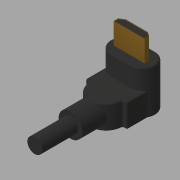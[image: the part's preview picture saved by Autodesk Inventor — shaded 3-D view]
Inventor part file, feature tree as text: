
AUTODESK INVENTOR PART (.ipt)
format: ipt  version: 2019 (Build 230136000, 136)  size: 250,880 bytes
history: native  units: mm
features: extrude x6, sketch x6, projected_geometry x3, other x2, fillet x1
ambient origin geometry x8: Origin, YZ Plane, XZ Plane, XY Plane, X Axis, Y Axis, Z Axis, Center Point
bodies: Solid1 (feature_tree), Solid2 (feature_tree)
feature tree (18):
  extrude  "Extrusion1"  Depth=7.0mm
  extrude  "Extrusion2"  Depth=15.0mm
  fillet  "Fillet1"  Radius=8.25mm
  extrude  "Extrusion3"  Depth=11.0mm
  extrude  "Extrusion4"  Depth=15.0mm
  extrude  "Extrusion5"  Depth=4.125mm
  extrude  "Extrusion6"  Depth=0.5mm
  other  "Work Axis1"
  sketch  "Sketch1"  dims[d0=14.0mm d1=7.0mm]
  sketch  "Sketch2"  dims[d2=2.0mm d3=15.0mm d4=8.25mm]
  sketch  "Sketch3"  dims[d5=4.125mm d6=11.0mm]
  projected_geometry  "Projected Loop1"
  sketch  "Sketch4"  dims[d7=8.0mm d8=0.0mm d9=15.0mm]
  sketch  "Sketch5"  dims[d10=8.25mm d11=4.125mm]
  projected_geometry  "Projected Loop2"
  sketch  "Sketch6"  dims[d12=6.66mm d13=0.0mm d14=0.5mm d15=8.0mm d16=12.0mm d17=0.0mm d18=5.0mm d19=12.0mm d20=0.0mm d21=10.42mm d22=2.5mm d24=1.5mm d25=1.5mm d26=1.5mm d27=1.5mm d28=7.15mm d29=0.0mm d30=0.15mm d31=0.15mm d32=0.0mm]
  projected_geometry  "Projected Loop3"
  other  "Work Point1"
